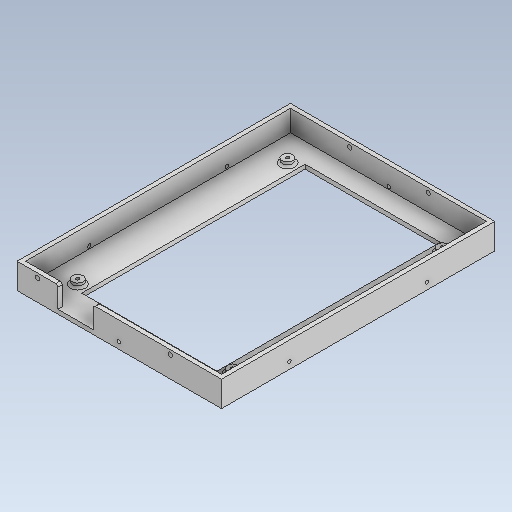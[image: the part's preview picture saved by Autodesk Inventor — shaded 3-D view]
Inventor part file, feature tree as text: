
AUTODESK INVENTOR PART (.ipt)
format: ipt  version: 2020.2 (Build 242310000, 310)  size: 223,744 bytes
history: native  units: in
note: dims shown in document units (in); Inventor stores cm internally (conversion verified against a paired STEP export)
features: sketch x11, hole x10, other x3, extrude x1, fillet x1
ambient origin geometry x8: Origin, YZ Plane, XZ Plane, XY Plane, X Axis, Y Axis, Z Axis, Center Point
bodies: Solid1 (feature_tree)
feature tree (26):
  other  "Back_Case.ipt"
  hole  "Hole3"  [1 undecoded]
  hole  "Hole4"  [1 undecoded]
  hole  "Hole5"  [1 undecoded]
  hole  "Hole6"  [1 undecoded]
  hole  "Hole7"  [1 undecoded]
  hole  "Hole8"  [1 undecoded]
  extrude  "Extrusion2"  Depth=0.625in
  fillet  "Fillet2"  Radius=1.2in
  hole  "Hole9"  [1 undecoded]
  hole  "Hole10"  [1 undecoded]
  hole  "Hole11"  [1 undecoded]
  hole  "Hole12"  [1 undecoded]
  other  "Inner Case::Back_Case.ipt"
  other  "TaggingFeature1"
  sketch  "Sketch3"  dims[d0=0.3937in d15=0.2in]
  sketch  "Sketch4"  dims[d16=3.0in]
  sketch  "Sketch5"  dims[d17=0.1in d18=0.315in d19=0.37in d20=0.25in d21=90.0deg d22=0.465in d23=0.0in d24=0.2in]
  sketch  "Sketch6"  dims[d25=3.0in]
  sketch  "Sketch7"  dims[d26=0.1in d27=0.315in d28=0.37in d29=0.25in d30=90.0deg d31=0.465in d32=0.0in d33=0.2in]
  sketch  "Sketch8"  dims[d34=2.0in]
  sketch  "Sketch10"  dims[d35=0.1in d36=0.315in d37=0.37in d38=0.25in d39=90.0deg d40=0.465in d41=0.0in d42=0.2in]
  sketch  "Sketch11"  dims[d43=2.0in]
  sketch  "Sketch12"  dims[d44=0.1in d45=0.315in d46=0.37in d47=0.25in d48=90.0deg d49=0.465in d50=0.0in d51=0.2in]
  sketch  "Sketch13"  dims[d52=2.0in]
  sketch  "Sketch14"  dims[d53=0.1in d54=0.315in d55=0.37in d56=0.25in d57=90.0deg d58=0.465in d59=0.0in d60=0.2in d61=2.0in d62=0.1in d63=0.315in d64=0.37in d65=0.25in d66=90.0deg d67=0.465in d68=0.0in d74=1.2in d75=1.05in d76=0.125in d77=0.0in d78=0.0612in d79=0.625in d80=1.84in d81=0.1276in d82=0.315in d83=0.375in d84=0.25in d85=0.5635in d86=0.465in d87=0.0in d88=0.625in d89=1.87in d90=0.1276in d91=0.315in d92=0.375in d93=0.25in d94=0.5635in d95=0.465in d96=0.0in d97=0.625in d98=1.5105in d99=0.1276in d100=0.315in d101=0.375in d102=0.25in d103=0.5635in d104=0.465in d105=0.0in d106=0.6in d107=0.625in d108=0.1276in d109=0.315in d110=0.375in d111=0.25in d112=0.5635in d113=0.465in d114=0.0in]
note: 10 required parameter values undecoded (feature->parameter linkage not recoverable at this tier; creation-order binding heuristic only, values carry confidence <= 0.55)
